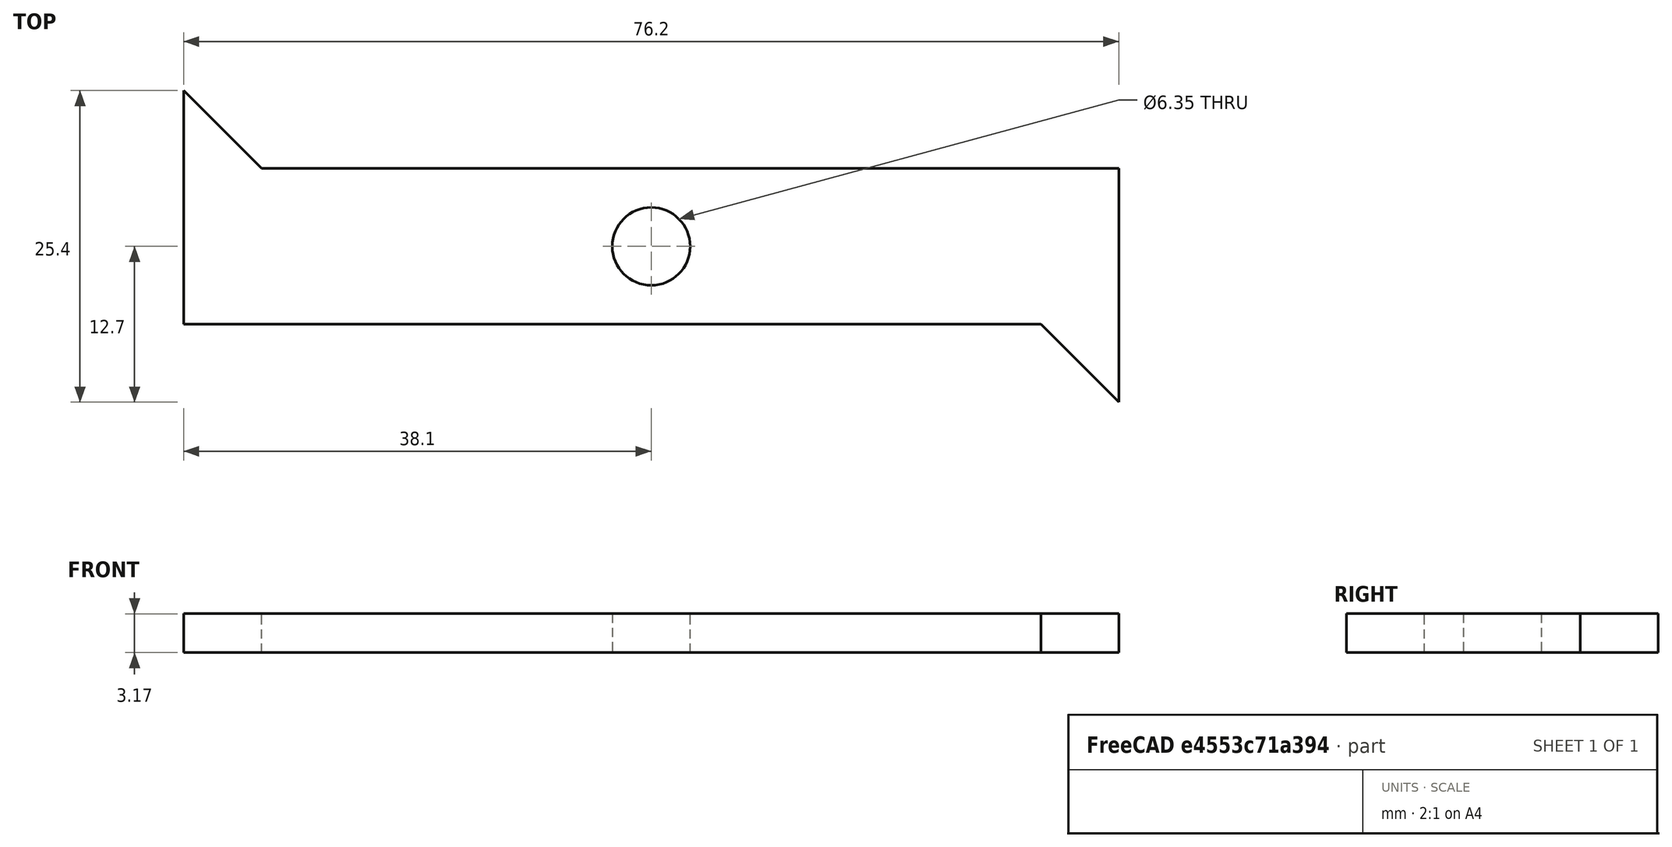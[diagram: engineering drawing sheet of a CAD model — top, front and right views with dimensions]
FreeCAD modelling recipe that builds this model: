
FCSTD DOCUMENT  (FreeCAD 0.15R4671 (Git))
Label: weapon_bar
License: All rights reserved
LicenseURL: http://en.wikipedia.org/wiki/All_rights_reserved
objects: Sketcher::SketchObject×1, PartDesign::Pad×1
note: 3 computed .brp shape members not serialized (recipe doc carries the construction recipe); baked Part::Feature solids carry a one-line shape summary decoded from their .brp

FEATURE [Sketcher::SketchObject] Sketch001
  sketch-geometry (9):
    g0: LineSegment StartX=-31.75 StartY=6.35 StartZ=0 EndX=38.1 EndY=6.35 EndZ=0
    g1: LineSegment StartX=38.1 StartY=6.35 StartZ=0 EndX=38.1 EndY=-6.35 EndZ=0
    g2: LineSegment StartX=31.75 StartY=-6.35 StartZ=0 EndX=-38.1 EndY=-6.35 EndZ=0
    g3: LineSegment StartX=-38.1 StartY=-6.35 StartZ=0 EndX=-38.1 EndY=6.35 EndZ=0
    g4: Circle CenterX=0 CenterY=0 CenterZ=0 NormalX=0 NormalY=0 NormalZ=1 Radius=3.175
    g5: LineSegment StartX=38.1 StartY=-6.35 StartZ=0 EndX=38.1 EndY=-12.7 EndZ=0
    g6: LineSegment StartX=31.75 StartY=-6.35 StartZ=0 EndX=38.1 EndY=-12.7 EndZ=0
    g7: LineSegment StartX=-38.1 StartY=6.35 StartZ=0 EndX=-38.1 EndY=12.7 EndZ=0
    g8: LineSegment StartX=-38.1 StartY=12.7 StartZ=0 EndX=-31.75 EndY=6.35 EndZ=0
  constraints (27):
    c: Coincident(g0,g1)
    c: Coincident(g2,g3)
    c: Horizontal(g0)
    c: Horizontal(g2)
    c: Vertical(g1)
    c: Vertical(g3)
    c: DistanceY(g3,g3) = -12.7
    c: DistanceX(g3,g0) = 76.2
    c: Radius(g4) = 3.175
    c: Coincident(g-1,g4)
    c: DistanceX(g6,g1) = 6.35
    c: Coincident(g5,g1)
    c: Vertical(g5)
    c: DistanceY(g1,g5) = -6.35
    c: Coincident(g6,g5)
    c: PointOnObject(g2,g6)
    c: PointOnObject(g8,g0)
    c: DistanceX(g8,g3) = -6.35
    c: Coincident(g7,g3)
    c: Vertical(g7)
    c: DistanceY(g7,g3) = -6.35
    c: Coincident(g8,g7)
    c: PointOnObject(g0,g8)
    c: Symmetric(g2,g0,g-1)
    c: DistanceY(g2,g0) = 12.7
    c: Coincident(g2,g6)
    c: DistanceY(g1,g0) = 12.7
FEATURE [PartDesign::Pad] Pad
  Length = 3.175
  Length2 = 100
  Sketch = -> Sketch001
  Type = 0
